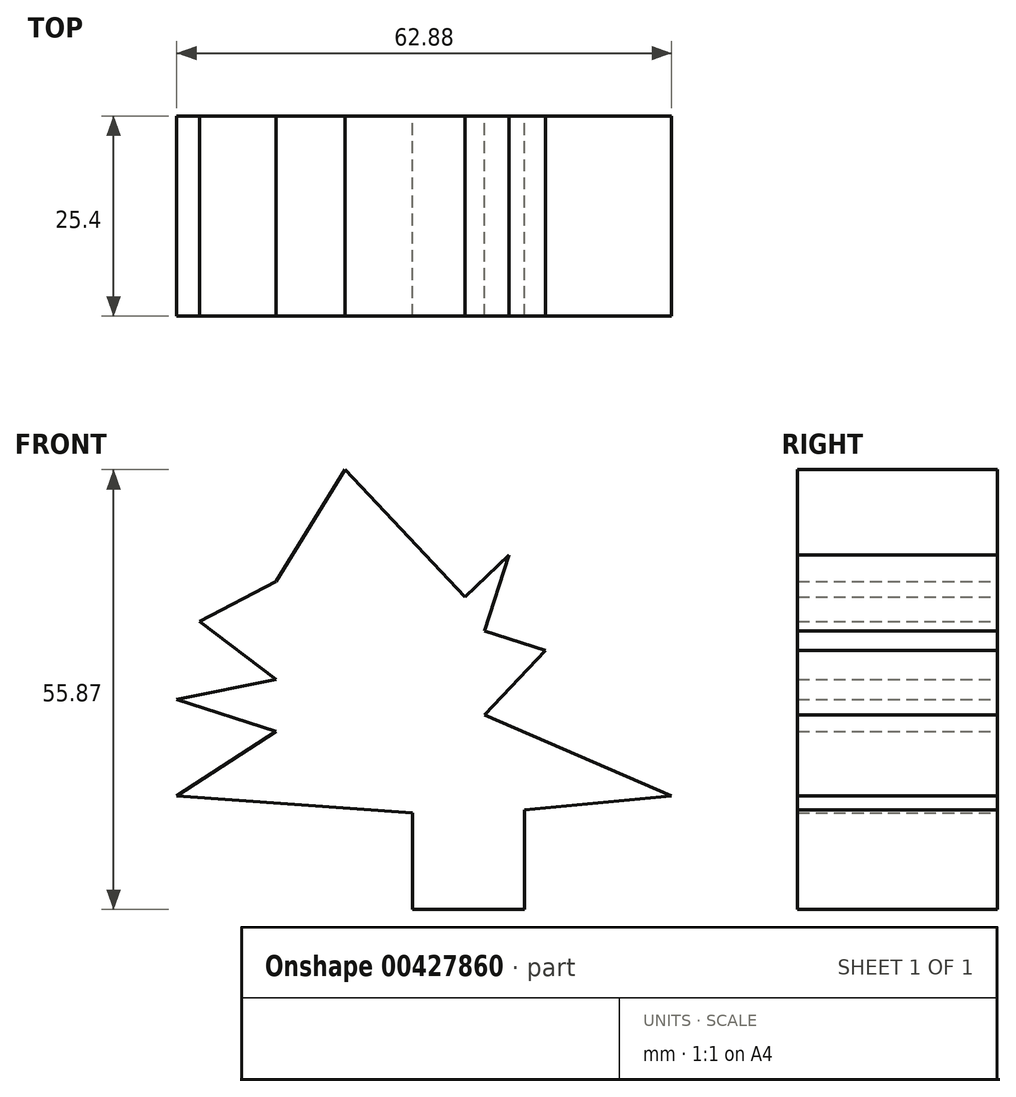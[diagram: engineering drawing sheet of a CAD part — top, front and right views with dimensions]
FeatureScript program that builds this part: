
annotation { "Feature Type Name" : "Feature", "Feature Type Description" : "" }
export const myFeature = defineFeature(function(context is Context, id is Id, definition is map)
    precondition{}
    {
        {
            var Q0;
            Q0=qCreatedBy(makeId("Front.planeOp"),FACE);
            var sketch = newSketch(context, id + "F0", { "sketchPlane" : qUnion([Q0])});
            skLineSegment(sketch, "E0", {"start": v(-9.15, -14.4) * mm, "end": v(-9.15, -26.67) * mm});
            skLineSegment(sketch, "E1", {"start": v(-9.15, -26.67) * mm, "end": v(5.06, -26.67) * mm});
            skLineSegment(sketch, "E2", {"start": v(5.06, -26.67) * mm, "end": v(5.06, -14.02) * mm});
            skLineSegment(sketch, "E3", {"start": v(-9.15, -14.4) * mm, "end": v(3.11, -14.4) * mm});
            skLineSegment(sketch, "E4", {"start": v(3.11, -14.4) * mm, "end": v(5.06, -14.02) * mm});
            skLineSegment(sketch, "E5", {"start": v(-9.15, -14.4) * mm, "end": v(-39.13, -12.26) * mm});
            skLineSegment(sketch, "E6", {"start": v(-39.13, -12.26) * mm, "end": v(-26.48, -4.09) * mm});
            skLineSegment(sketch, "E7", {"start": v(-26.48, -4.09) * mm, "end": v(-39.13, 0) * mm});
            skLineSegment(sketch, "E8", {"start": v(-39.13, 0) * mm, "end": v(-26.48, 2.53) * mm});
            skLineSegment(sketch, "E9", {"start": v(-26.48, 2.53) * mm, "end": v(-36.2, 9.93) * mm});
            skLineSegment(sketch, "E10", {"start": v(-36.2, 9.93) * mm, "end": v(-26.48, 14.99) * mm});
            skLineSegment(sketch, "E11", {"start": v(-26.48, 14.99) * mm, "end": v(-17.72, 29.2) * mm});
            skLineSegment(sketch, "E12", {"start": v(-17.72, 29.2) * mm, "end": v(-2.53, 13.04) * mm});
            skLineSegment(sketch, "E13", {"start": v(-2.53, 13.04) * mm, "end": v(3.11, 18.35) * mm});
            skLineSegment(sketch, "E14", {"start": v(3.11, 18.35) * mm, "end": v(0, 8.7) * mm});
            skLineSegment(sketch, "E15", {"start": v(0, 8.7) * mm, "end": v(7.71, 6.22) * mm});
            skLineSegment(sketch, "E16", {"start": v(7.71, 6.22) * mm, "end": v(0, -1.95) * mm});
            skLineSegment(sketch, "E17", {"start": v(0, -1.95) * mm, "end": v(23.75, -12.26) * mm});
            skLineSegment(sketch, "E18", {"start": v(23.75, -12.26) * mm, "end": v(5.06, -14.02) * mm});
            skSolve(sketch);
        }
        {
            var Q0;
            Q0=makeQuery(id+"F0.imprint","IMPRINT",FACE,{"disambiguationData":[TD([[makeQuery(id+"F0.imprint","IMPRINT",EDGE,{"derivedFrom":sQuery(id+"F0.wireOp",EDGE,"E0")}),1.0]])]});
            extrude(context, id + "F1", {"entities" : qUnion([Q0]), "depth" : 25.4 * mm});
        }
        {
            var Q0;
            Q0 = qSketchRegion(id + "F0", true);
            extrude(context, id + "F2", {"entities" : qUnion([Q0]), "operationType" : NewBodyOperationType.ADD, "depth" : 25.4 * mm});
        }
    });
